# Revit family: 304_Cim790 _-_
name_source: partatom
category: Pipe Accessories
revit_build: Autodesk Revit 2017 (Build: 20160225_1515(x64)
units: mm (PartAtom-declared; Revit-internal decimal feet)

## family parameters
Always vertical = Yes
Cut with Voids When Loaded = No
Part Type = Valve - Breaks Into
Round Connector Dimension = Use Diameter
Shared = No
Work Plane-Based = No

## types (14) — shared parameters
CAT0 = Yes
DD3 = 8 mm  [stored 0.0262467 ft]
Description = AUTOMATIC BALANCING VALVE - PN 25
L2D_Min = 3048 mm
Manufacturer = Cimberio
QmdConnectorList = 301;D;302;D
URL = www.cimberio.it
magiPartTypeId = 304
magiProductFamilyId = Cim790 *-*
zero-valued in all types: MC_Default_elevation

## per-type parameters (varying)
| type | A1 | A1__ve | CenSd_R1_6 | D | DD2 | DL | DL__ve | HH1 | HH2 | HH3 | HH4 | L2D | LL1 | LL3 | LL4 | LL5 | LL6 | R1 | W2D | ZZ1 | magiProductId |
| Cim790-15 (max 600 kPa) | 64 mm | -64 mm | 11 mm | 15 mm | 20 mm  [stored 0.0656168 ft] | 12 mm  [stored 0.0393701 ft] | -12 mm  [stored -0.0393701 ft] | 26 mm  [stored 0.0853018 ft] | 61 mm | 72 mm | 62 mm | 78 mm | 39 mm | 14 mm  [stored 0.0459318 ft] | 31 mm | 11 mm | 16 mm | 13 mm | 15 mm  [stored 0.0492126 ft] | 13 mm | Cim790 HF-15 |
| Cim790-50 (max 350 kPa) | 77 mm | -77 mm | 28 mm | 50 mm | 51 mm | 21 mm  [stored 0.0688976 ft] | -21 mm  [stored -0.0688976 ft] | 31 mm | 69 mm | 99 mm | 85 mm | 132 mm | 66 mm | 6 mm  [stored 0.019685 ft] | 35 mm | 14 mm  [stored 0.0459318 ft] | 26 mm  [stored 0.0853018 ft] | 32 mm  [stored 0.104987 ft] | 50 mm | 16 mm | Cim790 LF-50 |
| Cim790-40 (max 350 kPa) | 81 mm | -81 mm | 23 mm  [stored 0.0754593 ft] | 40 mm | 42 mm | 17 mm  [stored 0.0557743 ft] | -17 mm  [stored -0.0557743 ft] | 33 mm | 73 mm | 99 mm | 85 mm | 123 mm | 62 mm | 9 mm | 37 mm | 16 mm | 25 mm  [stored 0.082021 ft] | 26 mm  [stored 0.0853018 ft] | 40 mm | 17 mm  [stored 0.0557743 ft] | Cim790 LF-40 |
| Cim790-32 (max 350 kPa) | 83 mm | -83 mm | 20 mm  [stored 0.0656168 ft] | 32 mm | 37 mm | 17 mm  [stored 0.0557743 ft] | -17 mm  [stored -0.0557743 ft] | 34 mm | 78 mm | 99 mm | 85 mm | 123 mm | 62 mm | 7 mm  [stored 0.0229659 ft] | 40 mm | 9 mm | 25 mm  [stored 0.082021 ft] | 23 mm  [stored 0.0754593 ft] | 32 mm  [stored 0.104987 ft] | 17 mm  [stored 0.0557743 ft] | Cim790 LF-32 |
| Cim790-25L (max 350 kPa) | 85 mm | -85 mm | 17 mm  [stored 0.0557743 ft] | 25 mm | 32 mm  [stored 0.104987 ft] | 14 mm  [stored 0.0459318 ft] | -14 mm  [stored -0.0459318 ft] | 35 mm | 83 mm | 99 mm | 85 mm | 123 mm | 62 mm | 4 mm  [stored 0.0131234 ft] | 42 mm | 10 mm  [stored 0.0328084 ft] | 25 mm  [stored 0.082021 ft] | 20 mm  [stored 0.0656168 ft] | 25 mm  [stored 0.082021 ft] | 18 mm | Cim790 LF-25L |
| Cim790-25 (max 350 kPa) | 59 mm | -59 mm | 16 mm | 25 mm | 30 mm  [stored 0.0984252 ft] | 14 mm  [stored 0.0459318 ft] | -14 mm  [stored -0.0459318 ft] | 24 mm | 53 mm | 72 mm | 62 mm | 85 mm | 43 mm | 2 mm  [stored 0.00656168 ft] | 27 mm  [stored 0.0885827 ft] | 9 mm | 17 mm  [stored 0.0557743 ft] | 19 mm  [stored 0.062336 ft] | 25 mm  [stored 0.082021 ft] | 12 mm  [stored 0.0393701 ft] | Cim790 LF-25 |
| Cim790-20 (max 350 kPa) | 62 mm | -62 mm | 13 mm | 20 mm | 25 mm  [stored 0.082021 ft] | 12 mm  [stored 0.0393701 ft] | -12 mm  [stored -0.0393701 ft] | 25 mm  [stored 0.082021 ft] | 56 mm | 72 mm | 62 mm | 78 mm | 39 mm | 9 mm | 29 mm | 11 mm | 16 mm | 16 mm | 20 mm  [stored 0.0656168 ft] | 13 mm | Cim790 LF-20 |
| Cim790-15 (max 350 kPa) | 64 mm | -64 mm | 11 mm | 15 mm | 20 mm  [stored 0.0656168 ft] | 12 mm  [stored 0.0393701 ft] | -12 mm  [stored -0.0393701 ft] | 26 mm  [stored 0.0853018 ft] | 61 mm | 72 mm | 62 mm | 78 mm | 39 mm | 14 mm  [stored 0.0459318 ft] | 31 mm | 11 mm | 16 mm | 13 mm | 15 mm  [stored 0.0492126 ft] | 13 mm | Cim790 LF-15 |
| Cim790-50 (max 600 kPa) | 77 mm | -77 mm | 28 mm | 50 mm | 51 mm | 21 mm  [stored 0.0688976 ft] | -21 mm  [stored -0.0688976 ft] | 31 mm | 69 mm | 99 mm | 85 mm | 132 mm | 66 mm | 6 mm  [stored 0.019685 ft] | 35 mm | 14 mm  [stored 0.0459318 ft] | 26 mm  [stored 0.0853018 ft] | 32 mm  [stored 0.104987 ft] | 50 mm | 16 mm | Cim790 HF-50 |
| Cim790-40 (max 600 kPa) | 81 mm | -81 mm | 23 mm  [stored 0.0754593 ft] | 40 mm | 42 mm | 17 mm  [stored 0.0557743 ft] | -17 mm  [stored -0.0557743 ft] | 33 mm | 73 mm | 99 mm | 85 mm | 123 mm | 62 mm | 9 mm | 37 mm | 16 mm | 25 mm  [stored 0.082021 ft] | 26 mm  [stored 0.0853018 ft] | 40 mm | 17 mm  [stored 0.0557743 ft] | Cim790 HF-40 |
| Cim790-32 (max 600 kPa) | 83 mm | -83 mm | 20 mm  [stored 0.0656168 ft] | 32 mm | 37 mm | 17 mm  [stored 0.0557743 ft] | -17 mm  [stored -0.0557743 ft] | 34 mm | 78 mm | 99 mm | 85 mm | 123 mm | 62 mm | 7 mm  [stored 0.0229659 ft] | 40 mm | 9 mm | 25 mm  [stored 0.082021 ft] | 23 mm  [stored 0.0754593 ft] | 32 mm  [stored 0.104987 ft] | 17 mm  [stored 0.0557743 ft] | Cim790 HF-32 |
| Cim790-25L (max 600 kPa) | 85 mm | -85 mm | 17 mm  [stored 0.0557743 ft] | 25 mm | 32 mm  [stored 0.104987 ft] | 14 mm  [stored 0.0459318 ft] | -14 mm  [stored -0.0459318 ft] | 35 mm | 83 mm | 99 mm | 85 mm | 123 mm | 62 mm | 4 mm  [stored 0.0131234 ft] | 42 mm | 10 mm  [stored 0.0328084 ft] | 25 mm  [stored 0.082021 ft] | 20 mm  [stored 0.0656168 ft] | 25 mm  [stored 0.082021 ft] | 18 mm | Cim790 HF-25L |
| Cim790-25 (max 600 kPa) | 59 mm | -59 mm | 16 mm | 25 mm | 30 mm  [stored 0.0984252 ft] | 14 mm  [stored 0.0459318 ft] | -14 mm  [stored -0.0459318 ft] | 24 mm | 53 mm | 72 mm | 62 mm | 85 mm | 43 mm | 2 mm  [stored 0.00656168 ft] | 27 mm  [stored 0.0885827 ft] | 9 mm | 17 mm  [stored 0.0557743 ft] | 19 mm  [stored 0.062336 ft] | 25 mm  [stored 0.082021 ft] | 12 mm  [stored 0.0393701 ft] | Cim790 HF-25 |
| Cim790-20 (max 600 kPa) | 62 mm | -62 mm | 13 mm | 20 mm | 25 mm  [stored 0.082021 ft] | 12 mm  [stored 0.0393701 ft] | -12 mm  [stored -0.0393701 ft] | 25 mm  [stored 0.082021 ft] | 56 mm | 72 mm | 62 mm | 78 mm | 39 mm | 9 mm | 29 mm | 11 mm | 16 mm | 16 mm | 20 mm  [stored 0.0656168 ft] | 13 mm | Cim790 HF-20 |

note: column(s) folded — value = type name in every type: magiProductCode

note: [stored X ft] marks values corroborated as IEEE doubles in the binary element streams (Revit-internal decimal feet)

## geometry (parser evidence)
native form markers: Sweep x2
no freeform markers — native parametric forms only
